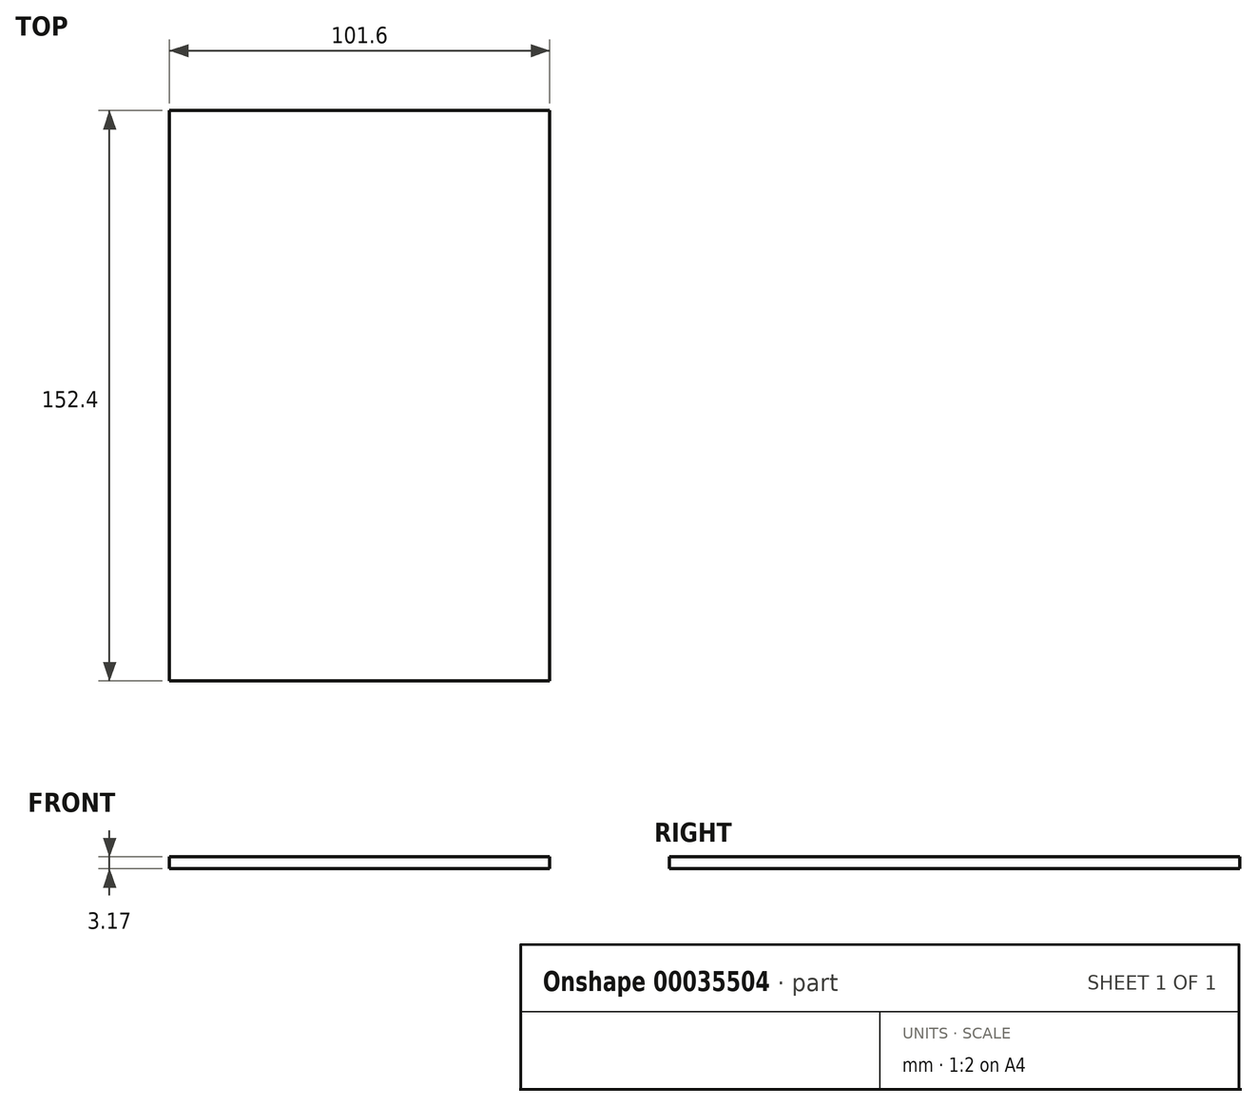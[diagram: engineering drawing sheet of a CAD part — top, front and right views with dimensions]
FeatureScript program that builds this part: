
annotation { "Feature Type Name" : "Feature", "Feature Type Description" : "" }
export const myFeature = defineFeature(function(context is Context, id is Id, definition is map)
    precondition{}
    {
        {
            var Q0;
            Q0=qCreatedBy(makeId("Top.planeOp"),FACE);
            var sketch = newSketch(context, id + "F0", { "sketchPlane" : qUnion([Q0])});
            skLineSegment(sketch, "E0.rect.bottom", {"start": v(-50.8, 76.2) * mm, "end": v(50.8, 76.2) * mm});
            skLineSegment(sketch, "E0.rect.top", {"start": v(-50.8, -76.2) * mm, "end": v(50.8, -76.2) * mm});
            skLineSegment(sketch, "E0.rect.left", {"start": v(-50.8, 76.2) * mm, "end": v(-50.8, -76.2) * mm});
            skLineSegment(sketch, "E0.rect.right", {"start": v(50.8, 76.2) * mm, "end": v(50.8, -76.2) * mm});
            skPoint(sketch, "E0.rect.middle", {"position": v(0, 0) * mm});
            skSolve(sketch);
        }
        {
            var Q0;
            Q0=makeQuery(id+"F0.imprint","IMPRINT",FACE,{"disambiguationData":[TD([[makeQuery(id+"F0.imprint","IMPRINT",EDGE,{"derivedFrom":sQuery(id+"F0.wireOp",EDGE,"E0.rect.bottom")}),-1.0]])]});
            extrude(context, id + "F1", {"entities" : qUnion([Q0]), "depth" : 3.17 * mm});
        }
    });
